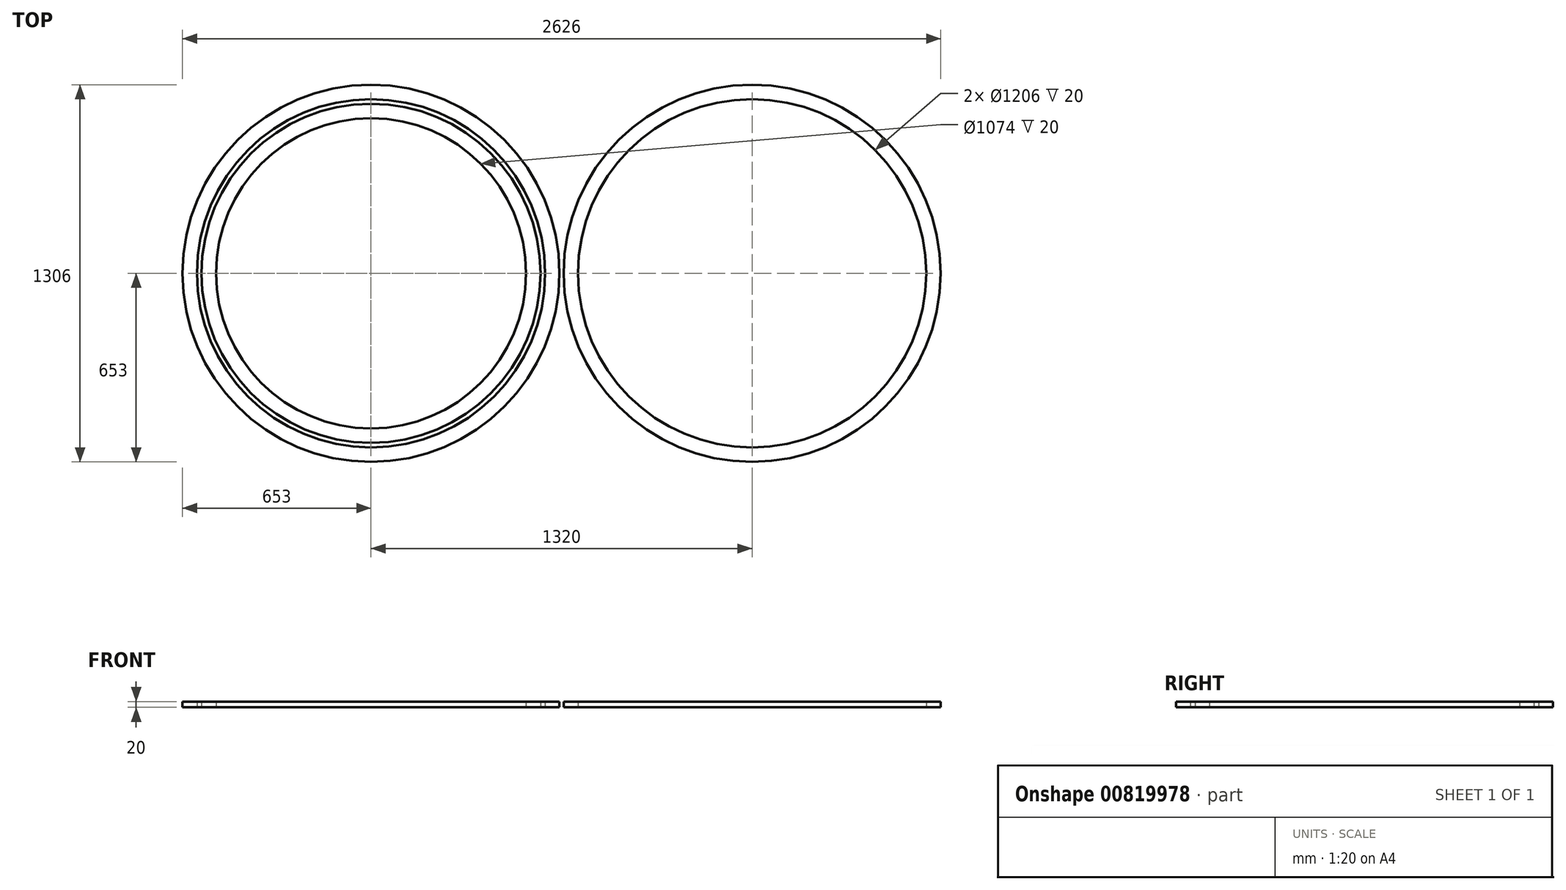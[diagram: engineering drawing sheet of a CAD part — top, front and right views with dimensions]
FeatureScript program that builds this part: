
annotation { "Feature Type Name" : "Feature", "Feature Type Description" : "" }
export const myFeature = defineFeature(function(context is Context, id is Id, definition is map)
    precondition{}
    {
        {
            var Q0;
            Q0=qCreatedBy(makeId("Top.planeOp"),FACE);
            var sketch = newSketch(context, id + "F0", { "sketchPlane" : qUnion([Q0])});
            skLineSegment(sketch, "E0.bottom", {"start": v(1320, -660) * mm, "end": v(-1320, -660) * mm});
            skLineSegment(sketch, "E0.top", {"start": v(1320, 660) * mm, "end": v(-1320, 660) * mm});
            skLineSegment(sketch, "E0.left", {"start": v(1320, -660) * mm, "end": v(1320, 660) * mm});
            skLineSegment(sketch, "E0.right", {"start": v(-1320, -660) * mm, "end": v(-1320, 660) * mm});
            skPoint(sketch, "E0.middle", {"position": v(0, 0) * mm});
            skLineSegment(sketch, "E1", {"start": v(-1320, -660) * mm, "end": v(-1320, 0) * mm});
            skLineSegment(sketch, "E2", {"start": v(-1320, 0) * mm, "end": v(-660, 0) * mm});
            skCircle(sketch, "E3", {"center": v(-660, 0) * mm, "radius": 653 * mm});
            skCircle(sketch, "E4", {"center": v(-660, 0) * mm, "radius": 603 * mm});
            skCircle(sketch, "E5", {"center": v(-660, 0) * mm, "radius": 587 * mm});
            skCircle(sketch, "E6", {"center": v(-660, 0) * mm, "radius": 537 * mm});
            skLineSegment(sketch, "E7", {"start": v(-660, 0) * mm, "end": v(660, 0) * mm});
            skCircle(sketch, "E8", {"center": v(660, 0) * mm, "radius": 653 * mm});
            skCircle(sketch, "E9", {"center": v(660, 0) * mm, "radius": 603 * mm});
            skSolve(sketch);
        }
        {
            var Q0;
            {var subQ5=sQuery(id+"F0.wireOp",EDGE,"E3");var subQ6=makeQuery(id+"F0.imprint","INTERSECT",VERTEX,{"derivedFrom":[sQuery(id+"F0.wireOp",EDGE,"E0.bottom"),subQ5]});Q0=makeQuery(id+"F0.imprint","IMPRINT",FACE,{"disambiguationData":[TD([[makeQuery(id+"F0.imprint","IMPRINT",EDGE,{"disambiguationData":[TD([[subQ6,-1.0]])],"derivedFrom":subQ5}),1.0]])]});}
            var Q1;
            {var subQ5=sQuery(id+"F0.wireOp",EDGE,"E3");var subQ6=makeQuery(id+"F0.imprint","INTERSECT",VERTEX,{"derivedFrom":[sQuery(id+"F0.wireOp",EDGE,"E0.top"),subQ5]});Q1=makeQuery(id+"F0.imprint","IMPRINT",FACE,{"disambiguationData":[TD([[makeQuery(id+"F0.imprint","IMPRINT",EDGE,{"disambiguationData":[TD([[subQ6,1.0]])],"derivedFrom":subQ5}),1.0]])]});}
            var Q2;
            Q2=makeQuery(id+"F0.imprint","IMPRINT",FACE,{"disambiguationData":[TD([[makeQuery(id+"F0.imprint","IMPRINT",EDGE,{"derivedFrom":sQuery(id+"F0.wireOp",EDGE,"E9")}),-1.0]])]});
            extrude(context, id + "F1", {"entities" : qUnion([Q0, Q1, Q2]), "depth" : 20 * mm, "offsetDistance" : 25 * mm});
        }
        {
            var Q0;
            {var subQ0=sQuery(id+"F0.wireOp",EDGE,"E5");var subQ1=sQuery(id+"F0.wireOp",EDGE,"E2");var subQ2=makeQuery(id+"F0.imprint","INTERSECT",VERTEX,{"derivedFrom":[subQ1,subQ0]});Q0=makeQuery(id+"F0.imprint","IMPRINT",FACE,{"disambiguationData":[TD([[makeQuery(id+"F0.imprint","IMPRINT",EDGE,{"disambiguationData":[TD([[subQ2,-1.0]])],"derivedFrom":subQ1}),1.0]])]});}
            var Q1;
            {var subQ0=sQuery(id+"F0.wireOp",EDGE,"E5");var subQ1=sQuery(id+"F0.wireOp",EDGE,"E2");var subQ2=makeQuery(id+"F0.imprint","INTERSECT",VERTEX,{"derivedFrom":[subQ1,subQ0]});Q1=makeQuery(id+"F0.imprint","IMPRINT",FACE,{"disambiguationData":[TD([[makeQuery(id+"F0.imprint","IMPRINT",EDGE,{"disambiguationData":[TD([[subQ2,-1.0]])],"derivedFrom":subQ1}),-1.0]])]});}
            var Q2;
            Q2=sQuery(id+"F0.wireOp",EDGE,"E6");
            var Q3;
            Q3=sQuery(id+"F0.wireOp",EDGE,"E5");
            extrude(context, id + "F2", {"entities" : qUnion([Q0, Q1]), "surfaceEntities" : qUnion([Q2, Q3]), "depth" : 20 * mm, "offsetDistance" : 25 * mm});
        }
    });
